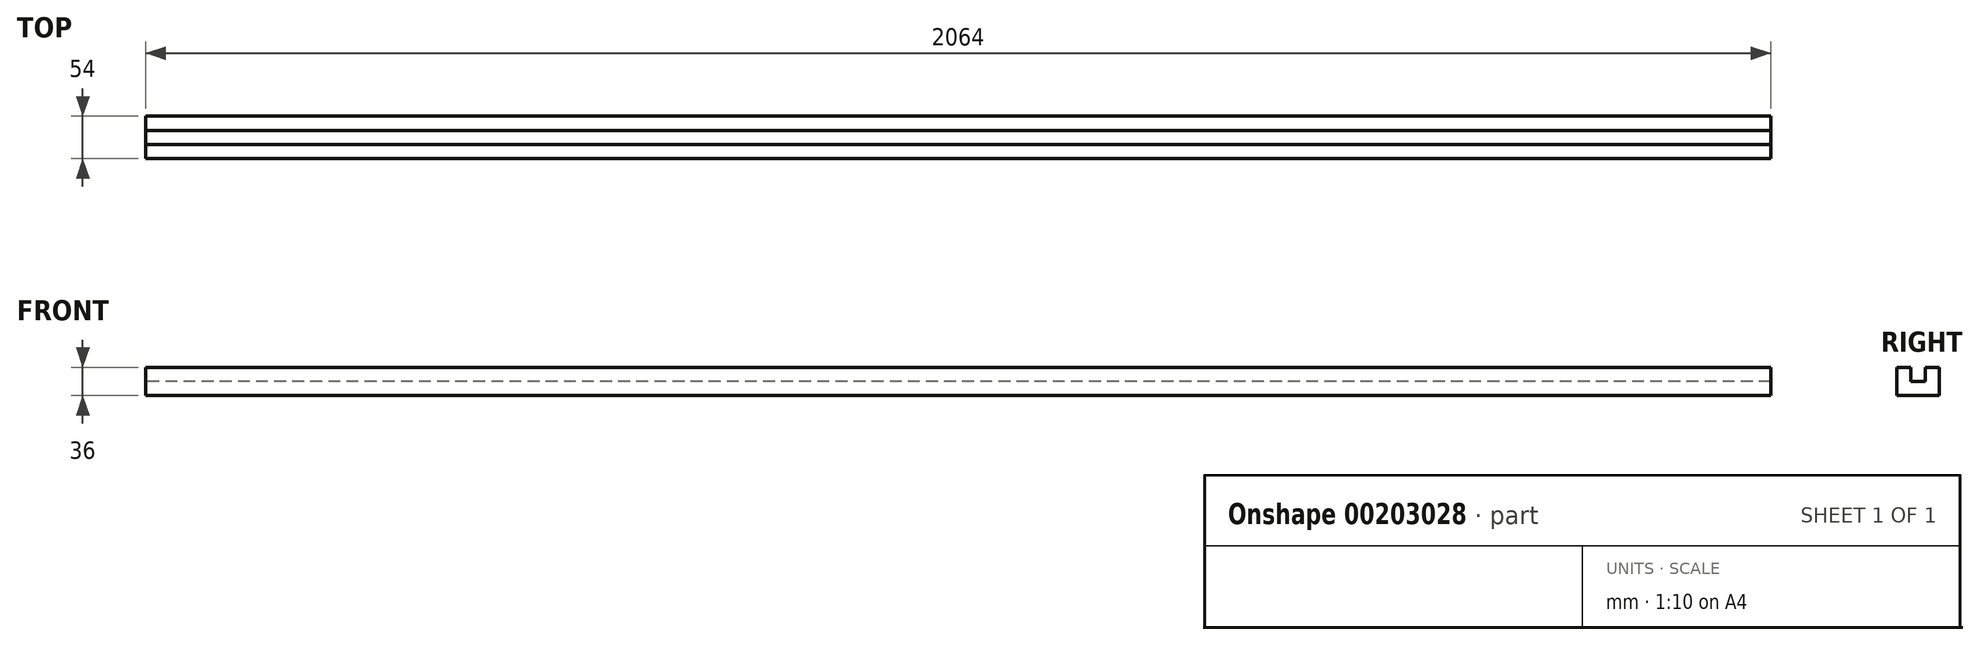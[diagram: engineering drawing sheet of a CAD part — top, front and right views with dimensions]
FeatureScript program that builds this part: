
annotation { "Feature Type Name" : "Feature", "Feature Type Description" : "" }
export const myFeature = defineFeature(function(context is Context, id is Id, definition is map)
    precondition{}
    {
        {
            var Q0;
            Q0=qCreatedBy(makeId("Right.planeOp"),FACE);
            var sketch = newSketch(context, id + "F0", { "sketchPlane" : qUnion([Q0])});
            skLineSegment(sketch, "E0", {"start": v(-28.51, 11.44) * mm, "end": v(-28.51, -24.36) * mm});
            skLineSegment(sketch, "E1", {"start": v(25.49, -24.36) * mm, "end": v(-28.51, -24.36) * mm});
            skLineSegment(sketch, "E2", {"start": v(25.49, 11.64) * mm, "end": v(7.49, 11.64) * mm});
            skLineSegment(sketch, "E3", {"start": v(7.49, 11.64) * mm, "end": v(7.49, -6.36) * mm});
            skLineSegment(sketch, "E4", {"start": v(7.49, -6.36) * mm, "end": v(-10.51, -6.36) * mm});
            skLineSegment(sketch, "E5", {"start": v(-10.51, -6.36) * mm, "end": v(-10.51, 11.64) * mm});
            skLineSegment(sketch, "E6", {"start": v(-10.51, 11.64) * mm, "end": v(-28.51, 11.44) * mm});
            skLineSegment(sketch, "E7", {"start": v(25.49, -24.36) * mm, "end": v(25.49, 11.64) * mm});
            skSolve(sketch);
        }
        {
            var Q0;
            Q0=makeQuery(id+"F0.imprint","IMPRINT",FACE,{"disambiguationData":[TD([[makeQuery(id+"F0.imprint","IMPRINT",EDGE,{"derivedFrom":sQuery(id+"F0.wireOp",EDGE,"E0")}),1.0]])]});
            extrude(context, id + "F1", {"entities" : qUnion([Q0]), "depth" : 2064 * mm});
        }
    });
